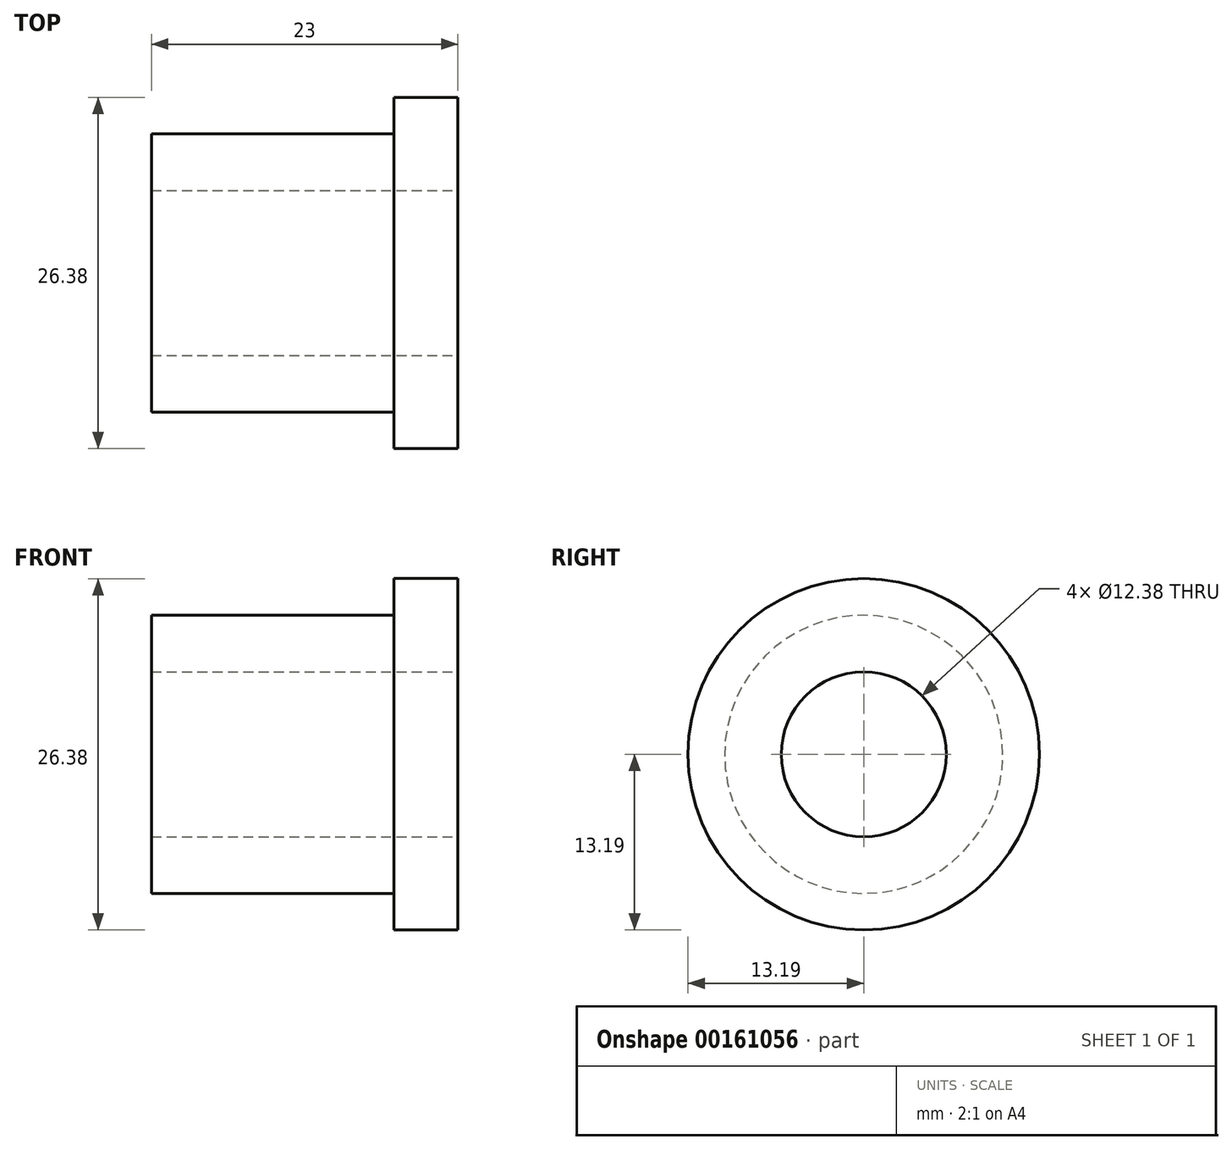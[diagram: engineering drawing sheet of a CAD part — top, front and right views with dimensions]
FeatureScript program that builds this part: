
annotation { "Feature Type Name" : "Feature", "Feature Type Description" : "" }
export const myFeature = defineFeature(function(context is Context, id is Id, definition is map)
    precondition{}
    {
        {
            var Q0;
            Q0=qCreatedBy(makeId("Front.planeOp"),FACE);
            var sketch = newSketch(context, id + "F0", { "sketchPlane" : qUnion([Q0])});
            skLineSegment(sketch, "E0", {"start": v(-15.91, 6.2) * mm, "end": v(7.09, 6.2) * mm});
            skLineSegment(sketch, "E1", {"start": v(7.09, 6.2) * mm, "end": v(7.09, 13.2) * mm});
            skLineSegment(sketch, "E2", {"start": v(7.09, 13.2) * mm, "end": v(2.29, 13.2) * mm});
            skLineSegment(sketch, "E3", {"start": v(2.29, 13.2) * mm, "end": v(2.29, 10.44) * mm});
            skLineSegment(sketch, "E4", {"start": v(2.29, 10.44) * mm, "end": v(-15.91, 10.44) * mm});
            skLineSegment(sketch, "E5", {"start": v(-15.91, 10.44) * mm, "end": v(-15.91, 6.2) * mm});
            skLineSegment(sketch, "E6.bottom", {"start": v(17.08, 0) * mm, "end": v(-59.05, 0) * mm});
            skSolve(sketch);
        }
        {
            var Q0;
            {var subQ1=sQuery(id+"F0.wireOp",EDGE,"E2");Q0=makeQuery(id+"F0.imprint","IMPRINT",FACE,{"disambiguationData":[TD([[makeQuery(id+"F0.imprint","IMPRINT",EDGE,{"derivedFrom":subQ1}),1.0]])]});}
            var Q1;
            Q1=sQuery(id+"F0.wireOp",EDGE,"E6.bottom");
            revolve(context, id + "F1", {"entities" : qUnion([Q0]), "axis" : qUnion([Q1]), "revolveType" : RevolveType.FULL});
        }
    });
